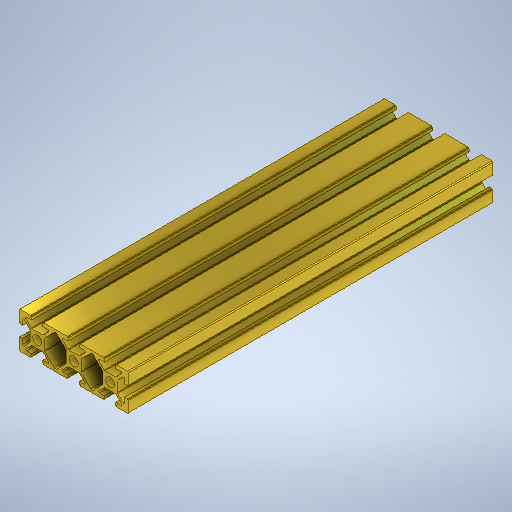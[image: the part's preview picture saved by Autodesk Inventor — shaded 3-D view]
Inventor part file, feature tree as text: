
AUTODESK INVENTOR PART (.ipt)
format: ipt  version: 2025.2 (Build 292293000, 293)  size: 504,832 bytes
history: native  units: mm
features: mirror x2, fillet x2, extrude x1, sketch x1
ambient origin geometry x8: Origin, YZ Plane, XZ Plane, XY Plane, X Axis, Y Axis, Z Axis, Center Point
bodies: Body1 (feature_tree)
feature tree (6):
  extrude  "Extrusão2"  Depth=60.0mm
  mirror  "Espelhar5"
  mirror  "Espelhar6"
  fillet  "Arredondamento3"  Radius=20.0mm
  fillet  "Arredondamento4"  Radius=6.2mm
  sketch  "Esboço2"  dims[d24=10.0mm d25=60.0mm d26=20.0mm d28=6.2mm d29=6.0mm d31=5.0mm d32=2.0mm d33=4.0mm d35=0.5mm d36=0.5mm d38=4.0mm d39=4.0mm d41=200.0mm d42=0.0mm d43=1.0mm d44=1.0mm]
